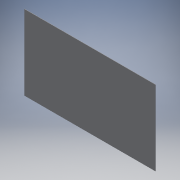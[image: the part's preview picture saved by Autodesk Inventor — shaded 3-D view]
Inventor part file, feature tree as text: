
AUTODESK INVENTOR PART (.ipt)
format: ipt  version: 2016 (Build 200138000, 138)  size: 84,480 bytes
history: native  units: in
note: dims shown in document units (in); Inventor stores cm internally (conversion verified against a paired STEP export)
features: extrude x1, sketch x1
ambient origin geometry x8: Origin, YZ Plane, XZ Plane, XY Plane, X Axis, Y Axis, Z Axis, Center Point
bodies: Solid1 (feature_tree)
feature tree (2):
  extrude  "Extrusion1"  Depth=11.75in
  sketch  "Sketch1"  dims[d0=21.0in d1=11.75in d2=0.0625in d3=0.0in]
